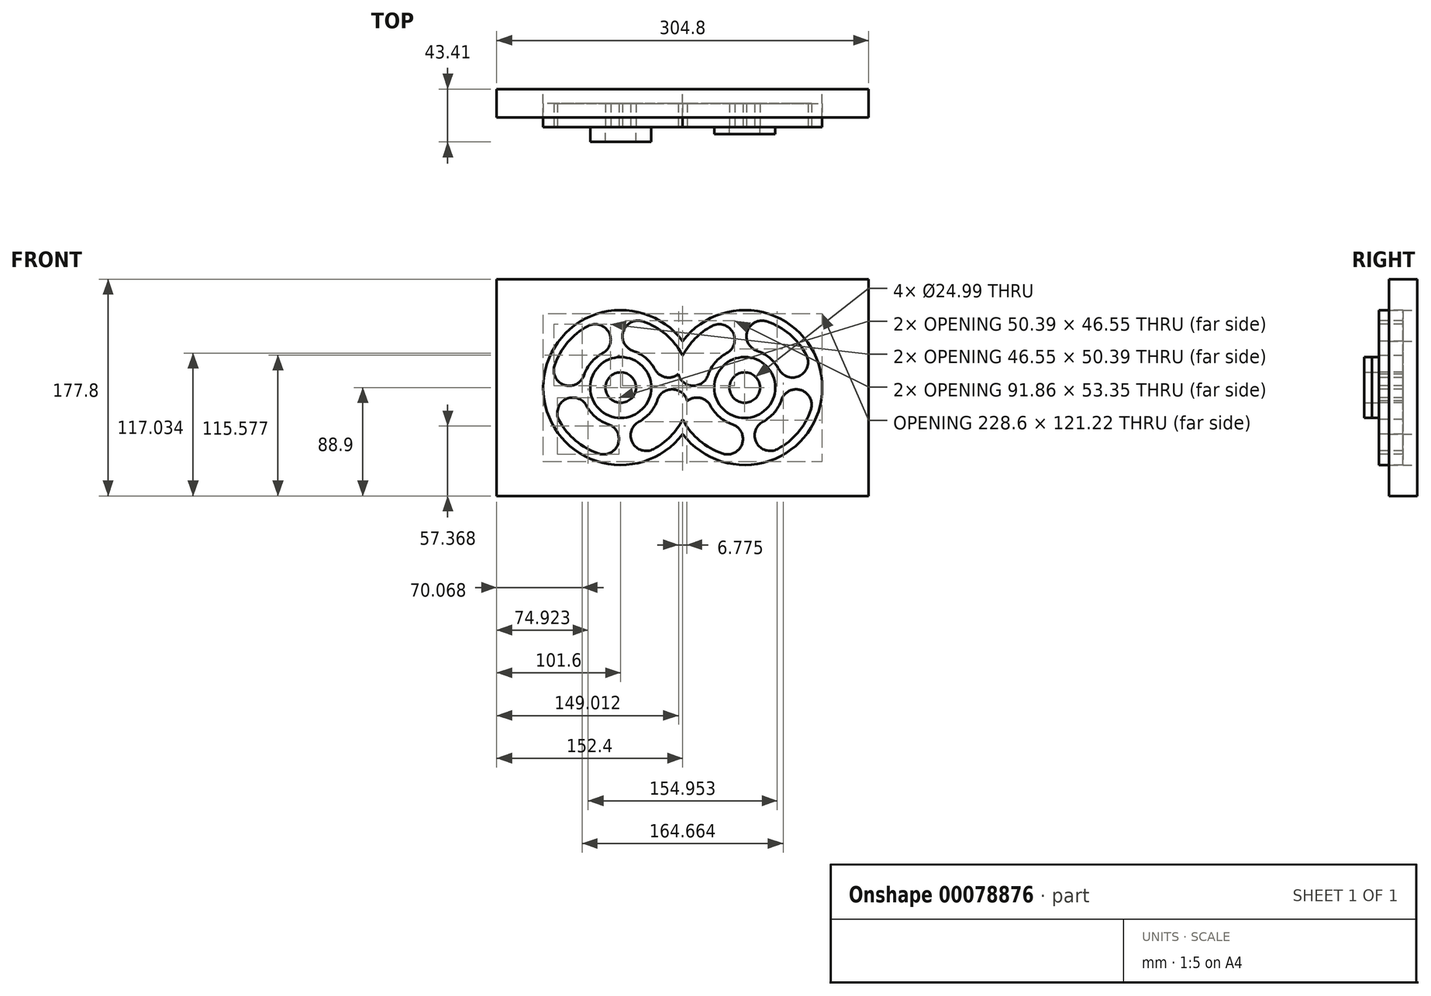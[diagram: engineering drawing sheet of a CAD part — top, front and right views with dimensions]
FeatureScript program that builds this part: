
annotation { "Feature Type Name" : "Feature", "Feature Type Description" : "" }
export const myFeature = defineFeature(function(context is Context, id is Id, definition is map)
    precondition{}
    {
        {
            var Q0;
            Q0=qCreatedBy(makeId("Front.planeOp"),FACE);
            var sketch = newSketch(context, id + "F0", { "sketchPlane" : qUnion([Q0])});
            skCircle(sketch, "E0", {"center": v(50.8, 0) * mm, "radius": 12.5 * mm});
            skCircle(sketch, "E1", {"center": v(-50.8, 0) * mm, "radius": 12.5 * mm});
            skCircle(sketch, "E2", {"center": v(-50.8, 0) * mm, "radius": 25 * mm});
            skCircle(sketch, "E3", {"center": v(50.8, 0) * mm, "radius": 25 * mm});
            skCircle(sketch, "E4", {"center": v(-50.8, 0) * mm, "radius": 63.5 * mm});
            skCircle(sketch, "E5", {"center": v(50.8, 0) * mm, "radius": 63.5 * mm});
            skLineSegment(sketch, "E6.bottom", {"start": v(-152.4, 88.9) * mm, "end": v(152.4, 88.9) * mm});
            skLineSegment(sketch, "E6.top", {"start": v(-152.4, -88.9) * mm, "end": v(152.4, -88.9) * mm});
            skLineSegment(sketch, "E6.left", {"start": v(-152.4, 88.9) * mm, "end": v(-152.4, -88.9) * mm});
            skLineSegment(sketch, "E6.right", {"start": v(152.4, 88.9) * mm, "end": v(152.4, -88.9) * mm});
            skPoint(sketch, "E7", {"position": v(-152.4, 0) * mm});
            skPoint(sketch, "E8", {"position": v(0, 88.9) * mm});
            skPoint(sketch, "E9", {"position": v(0, 38.1) * mm});
            skSolve(sketch);
        }
        {
            var Q0;
            Q0=makeQuery(id+"F0.imprint","IMPRINT",FACE,{"disambiguationData":[TD([[makeQuery(id+"F0.imprint","IMPRINT",EDGE,{"derivedFrom":sQuery(id+"F0.wireOp",EDGE,"E6.bottom")}),-1.0]])]});
            cPlane(context, id + "F1", {"entities" : qUnion([Q0]), "cplaneType" : CPlaneType.OFFSET, "offset" : 31.24 * mm, "oppositeDirection" : true, "width" : 152.4 * mm, "height" : 152.4 * mm});
        }
        {
            var Q0;
            Q0=qCreatedBy(id+"F1.planeOp",FACE);
            var sketch = newSketch(context, id + "F2", { "sketchPlane" : qUnion([Q0])});
            skLineSegment(sketch, "E10.bottom", {"start": v(-152.4, 88.9) * mm, "end": v(152.4, 88.9) * mm});
            skLineSegment(sketch, "E10.top", {"start": v(-152.4, -88.9) * mm, "end": v(152.4, -88.9) * mm});
            skLineSegment(sketch, "E10.left", {"start": v(-152.4, 88.9) * mm, "end": v(-152.4, -88.9) * mm});
            skLineSegment(sketch, "E10.right", {"start": v(152.4, 88.9) * mm, "end": v(152.4, -88.9) * mm});
            skPoint(sketch, "E11", {"position": v(0, 88.9) * mm});
            skPoint(sketch, "E12", {"position": v(152.4, 0) * mm});
            skCircle(sketch, "E13", {"center": v(-50.8, 0) * mm, "radius": 63.5 * mm});
            skCircle(sketch, "E14", {"center": v(50.8, 0) * mm, "radius": 63.5 * mm});
            skSolve(sketch);
        }
        {
            var Q0;
            Q0 = qSketchRegion(id + "F2", true);
            extrude(context, id + "F3", {"entities" : qUnion([Q0]), "depth" : 23.24 * mm});
        }
        {
            var Q0;
            Q0=makeQuery(id+"F0.imprint","IMPRINT",FACE,{"disambiguationData":[TD([[makeQuery(id+"F0.imprint","IMPRINT",EDGE,{"derivedFrom":sQuery(id+"F0.wireOp",EDGE,"E1")}),-1.0]])]});
            var Q1;
            Q1=makeQuery(id+"F0.imprint","IMPRINT",FACE,{"disambiguationData":[TD([[makeQuery(id+"F0.imprint","IMPRINT",EDGE,{"derivedFrom":sQuery(id+"F0.wireOp",EDGE,"E0")}),-1.0]])]});
            extrude(context, id + "F4", {"entities" : qUnion([Q0, Q1]), "depth" : 12.17 * mm});
        }
        {
            var Q0;
            Q0=makeQuery(id+"F0.imprint","IMPRINT",FACE,{"disambiguationData":[TD([[makeQuery(id+"F0.imprint","IMPRINT",EDGE,{"derivedFrom":sQuery(id+"F0.wireOp",EDGE,"E2")}),-1.0]])]});
            var Q1;
            Q1=makeQuery(id+"F0.imprint","IMPRINT",FACE,{"disambiguationData":[TD([[makeQuery(id+"F0.imprint","IMPRINT",EDGE,{"derivedFrom":sQuery(id+"F0.wireOp",EDGE,"E1")}),-1.0]])]});
            var Q2;
            Q2=makeQuery(id+"F0.imprint","IMPRINT",FACE,{"disambiguationData":[TD([[makeQuery(id+"F0.imprint","IMPRINT",EDGE,{"derivedFrom":sQuery(id+"F0.wireOp",EDGE,"E3")}),-1.0]])]});
            var Q3;
            Q3=makeQuery(id+"F0.imprint","IMPRINT",FACE,{"disambiguationData":[TD([[makeQuery(id+"F0.imprint","IMPRINT",EDGE,{"derivedFrom":sQuery(id+"F0.wireOp",EDGE,"E0")}),-1.0]])]});
            var Q4;
            {var subQ0=sQuery(id+"F0.wireOp",EDGE,"E5");var subQ1=sQuery(id+"F0.wireOp",EDGE,"E4");var subQ2=makeQuery(id+"F0.imprint","INTERSECT",VERTEX,{"disambiguationData":[OD(0.0)],"derivedFrom":[subQ1,subQ0]});Q4=makeQuery(id+"F0.imprint","IMPRINT",FACE,{"disambiguationData":[TD([[makeQuery(id+"F0.imprint","IMPRINT",EDGE,{"disambiguationData":[TD([[subQ2,-1.0]])],"derivedFrom":subQ1}),1.0]])]});}
            extrude(context, id + "F5", {"entities" : qUnion([Q0, Q1, Q2, Q3, Q4]), "oppositeDirection" : true, "depth" : 19.53 * mm});
        }
        {
            var Q0;
            Q0=qCreatedBy(makeId("Top.planeOp"),FACE);
            var sketch = newSketch(context, id + "F6", { "sketchPlane" : qUnion([Q0])});
            skLineSegment(sketch, "E15.bottom", {"start": v(0, -31.22) * mm, "end": v(127, -31.22) * mm});
            skLineSegment(sketch, "E15.top", {"start": v(0, -5.82) * mm, "end": v(127, -5.82) * mm});
            skLineSegment(sketch, "E15.left", {"start": v(0, -31.22) * mm, "end": v(0, -5.82) * mm});
            skLineSegment(sketch, "E15.right", {"start": v(127, -31.22) * mm, "end": v(127, -5.82) * mm});
            skSolve(sketch);
        }
        {
            var Q0;
            Q0=makeQuery(id+"F6.imprint","IMPRINT",FACE,{"disambiguationData":[TD([[makeQuery(id+"F6.imprint","IMPRINT",EDGE,{"derivedFrom":sQuery(id+"F6.wireOp",EDGE,"E15.bottom")}),1.0]])]});
            extrude(context, id + "F7", {"entities" : qUnion([Q0]), "operationType" : NewBodyOperationType.REMOVE, "oppositeDirection" : true, "depth" : 127 * mm, "hasSecondDirection" : true, "secondDirectionOppositeDirection" : false, "secondDirectionDepth" : 127 * mm});
        }
        {
            var Q0;
            Q0=qCreatedBy(makeId("Front.planeOp"),FACE);
            var sketch = newSketch(context, id + "F8", { "sketchPlane" : qUnion([Q0])});
            skPoint(sketch, "E16", {"position": v(-50.8, 0) * mm});
            skPoint(sketch, "E17", {"position": v(50.8, 0) * mm});
            skArc(sketch, "E18", {"start": v(-77.67, 50.44) * mm, "mid": v(-94.41, 36.93) * mm, "end": v(-104.98, 18.2) * mm});
            skArc(sketch, "E19", {"start": v(-65.73, 28.02) * mm, "mid": v(-75.03, 20.52) * mm, "end": v(-80.9, 10.1) * mm});
            skArc(sketch, "E20", {"start": v(-104.98, 18.2) * mm, "mid": v(-96.98, 2.11) * mm, "end": v(-80.9, 10.1) * mm});
            skArc(sketch, "E21", {"start": v(-65.73, 28.02) * mm, "mid": v(-60.49, 45.2) * mm, "end": v(-77.67, 50.44) * mm});
            skArc(sketch, "E22.1.0", {"start": v(-101.24, -26.87) * mm, "mid": v(-87.73, -43.61) * mm, "end": v(-69, -54.18) * mm});
            skArc(sketch, "E22.1.1", {"start": v(-69, -54.18) * mm, "mid": v(-52.91, -46.18) * mm, "end": v(-60.9, -30.1) * mm});
            skArc(sketch, "E22.1.2", {"start": v(-78.82, -14.93) * mm, "mid": v(-71.32, -24.23) * mm, "end": v(-60.9, -30.1) * mm});
            skArc(sketch, "E22.1.3", {"start": v(-78.82, -14.93) * mm, "mid": v(-96, -9.69) * mm, "end": v(-101.24, -26.87) * mm});
            skArc(sketch, "E22.2.0", {"start": v(-23.93, -50.44) * mm, "mid": v(-10.1, -40.13) * mm, "end": v(0.01, -26.16) * mm});
            skArc(sketch, "E22.2.1", {"start": v(3.63, -10.98) * mm, "mid": v(-8.2, -1.46) * mm, "end": v(-20.7, -10.1) * mm});
            skArc(sketch, "E22.2.2", {"start": v(-35.87, -28.02) * mm, "mid": v(-26.57, -20.52) * mm, "end": v(-20.7, -10.1) * mm});
            skArc(sketch, "E22.2.3", {"start": v(-35.87, -28.02) * mm, "mid": v(-41.11, -45.2) * mm, "end": v(-23.93, -50.44) * mm});
            skArc(sketch, "E22.3.0", {"start": v(-0.36, 26.87) * mm, "mid": v(-13.87, 43.61) * mm, "end": v(-32.6, 54.18) * mm});
            skArc(sketch, "E22.3.1", {"start": v(-32.6, 54.18) * mm, "mid": v(-48.69, 46.18) * mm, "end": v(-40.7, 30.1) * mm});
            skArc(sketch, "E22.3.2", {"start": v(-22.78, 14.93) * mm, "mid": v(-30.28, 24.23) * mm, "end": v(-40.7, 30.1) * mm});
            skArc(sketch, "E22.3.3", {"start": v(-22.78, 14.93) * mm, "mid": v(-14.13, 8.46) * mm, "end": v(-3.63, 10.98) * mm});
            skArc(sketch, "E23.1.0.0", {"start": v(0.36, -26.87) * mm, "mid": v(13.87, -43.61) * mm, "end": v(32.6, -54.18) * mm});
            skArc(sketch, "E23.1.0.1", {"start": v(22.78, -14.93) * mm, "mid": v(14.13, -8.46) * mm, "end": v(3.63, -10.98) * mm});
            skArc(sketch, "E23.1.0.2", {"start": v(32.6, -54.18) * mm, "mid": v(48.69, -46.18) * mm, "end": v(40.7, -30.1) * mm});
            skArc(sketch, "E23.1.0.3", {"start": v(69, 54.18) * mm, "mid": v(52.91, 46.18) * mm, "end": v(60.9, 30.1) * mm});
            skArc(sketch, "E23.1.0.4", {"start": v(104.98, -18.2) * mm, "mid": v(96.98, -2.11) * mm, "end": v(80.9, -10.1) * mm});
            skArc(sketch, "E23.1.0.5", {"start": v(35.87, 28.02) * mm, "mid": v(41.11, 45.2) * mm, "end": v(23.93, 50.44) * mm});
            skArc(sketch, "E23.1.0.6", {"start": v(78.82, 14.93) * mm, "mid": v(96, 9.69) * mm, "end": v(101.24, 26.87) * mm});
            skArc(sketch, "E23.1.0.7", {"start": v(22.78, -14.93) * mm, "mid": v(30.28, -24.23) * mm, "end": v(40.7, -30.1) * mm});
            skArc(sketch, "E23.1.0.8", {"start": v(78.82, 14.93) * mm, "mid": v(71.32, 24.23) * mm, "end": v(60.9, 30.1) * mm});
            skArc(sketch, "E23.1.0.9", {"start": v(-3.63, 10.98) * mm, "mid": v(8.2, 1.46) * mm, "end": v(20.7, 10.1) * mm});
            skArc(sketch, "E23.1.0.10", {"start": v(65.73, -28.02) * mm, "mid": v(75.03, -20.52) * mm, "end": v(80.9, -10.1) * mm});
            skArc(sketch, "E23.1.0.11", {"start": v(23.93, 50.44) * mm, "mid": v(10.1, 40.13) * mm, "end": v(-0.01, 26.16) * mm});
            skArc(sketch, "E23.1.0.13", {"start": v(35.87, 28.02) * mm, "mid": v(26.57, 20.52) * mm, "end": v(20.7, 10.1) * mm});
            skArc(sketch, "E23.1.0.14", {"start": v(65.73, -28.02) * mm, "mid": v(60.49, -45.2) * mm, "end": v(77.67, -50.44) * mm});
            skArc(sketch, "E23.1.0.15", {"start": v(101.24, 26.87) * mm, "mid": v(87.73, 43.61) * mm, "end": v(69, 54.18) * mm});
            skArc(sketch, "E23.1.0.16", {"start": v(77.67, -50.44) * mm, "mid": v(94.41, -36.93) * mm, "end": v(104.98, -18.2) * mm});
            skLineSegment(sketch, "E23.direction1", {"start": v(-101.24, -26.87) * mm, "end": v(0.36, -26.87) * mm, "construction": true});
            skPoint(sketch, "E24.orphan", {"position": v(-3.38, 18.2) * mm});
            skArc(sketch, "E25.trimOffspring", {"start": v(-0.01, 26.16) * mm, "mid": v(-0.18, 26.52) * mm, "end": v(-0.36, 26.87) * mm});
            skArc(sketch, "E26.trimOffspring", {"start": v(0.01, -26.16) * mm, "mid": v(0.18, -26.52) * mm, "end": v(0.36, -26.87) * mm});
            skPoint(sketch, "E27.orphan", {"position": v(3.38, -18.2) * mm});
            skSolve(sketch);
        }
        {
            var Q0;
            Q0 = qSketchRegion(id + "F8", true);
            extrude(context, id + "F9", {"entities" : qUnion([Q0]), "operationType" : NewBodyOperationType.REMOVE, "endBound" : BoundingType.THROUGH_ALL, "oppositeDirection" : true, "depth" : 25.4 * mm});
        }
    });
